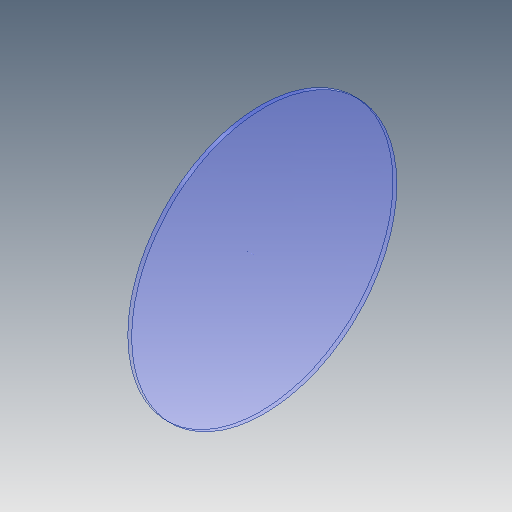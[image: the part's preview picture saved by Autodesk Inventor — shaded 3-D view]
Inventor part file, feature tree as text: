
AUTODESK INVENTOR PART (.ipt)
format: ipt  version: 2020.3 (Build 243373010, 373A)  size: 134,656 bytes
history: native  units: mm
features: revolve x1, sketch x1
ambient origin geometry x8: Origin, YZ Plane, XZ Plane, XY Plane, X Axis, Y Axis, Z Axis, Center Point
bodies: Solid1 (feature_tree)
feature tree (2):
  revolve  "Revolution1"  [1 undecoded]
  sketch  "Sketch1"  dims[d0=35.0mm d1=1.0mm d2=70.0mm d3=200.0mm d4=90.0deg]
note: 1 required parameter value undecoded (feature->parameter linkage not recoverable at this tier; creation-order binding heuristic only, values carry confidence <= 0.55)
